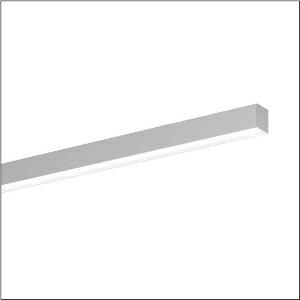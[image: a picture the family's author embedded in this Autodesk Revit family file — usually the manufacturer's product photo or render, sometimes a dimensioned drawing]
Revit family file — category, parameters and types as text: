
# Revit family: silica_r__21_51mx23da44sb_489f
name_source: partatom
category: Lighting Fixtures
units: mm (PartAtom-declared; Revit-internal decimal feet)

## family parameters
Cut with Voids When Loaded = No
Host = Face
Light Source = No
Part Type = Normal
Room Calculation Point = No
Round Connector Dimension = Use Diameter
Shared = No

## types (1)
- --- (1 x LED, 3280 lm, 22.4 W, 4000K)
    Apparent Load = 22 VA
    CIE Flux Codes = 78 96 99 100 100
    Color Rendering = 80
    Color Temperature = 4000K
    Default Elevation = 1800 mm
    Description = Silica® 21, office luminaire, primary optical cover: prismatic diffuser, of PMMA, CAT 2 (L<= 3000cd/m²), light emission: direct distribution, primary light characteristic: symmetric, installation type: surface-mounted, LED, rated luminous flux: 3.280lm, luminous efficacy: 146lm/W, light colour: 840, colour temperature: 4000K, with terminal, 3+2-pole, max. 2.5mm², mains connection: 220..240V, AC, 50/60Hz, rated input power: 22.4W, luminaire housing, of aluminium, metallic grey (RAL 9006), length: 1.204mm, width: 53mm, height: 53mm, protection rating (complete): IP20, insulation class (complete): insulation class I (protective earthing), certification: CE, permissible operating ambient temperature: 0..+35°C, standard: EN 50419, packaging unit: 1 piece
    Height = 0 mm  [stored 0 ft]
    Lamp = 1 x LED
    Lamp Light Flux = 3280 lm
    Lamp Power = 22.4 W
    Lamp count = 1
    Length = 1204 mm
    Luminous efficacy = 146 lm/W
    Manufacturer = Siteco
    ModVariant = No
    Model = 51MX23DA44SB
    Mounting Place = Ceiling
    Mounting Type = Recessed
    Number of Poles = 1
    OnlyDefault = Yes
    Power Factor = 1
    Product Name = Silica® 21
    Product group = office luminaire | ceiling recessed
    ProductGroupID = 401
    Protection Class = Protection class I
    Protection Degree = IP 20
    RLX_Detail_Level = 1
    RLX_Emergency_Light_Flux = 0 lm
    RLX_Emergency_Type = 0
    RLX_Emergency_Type_DB = No
    RlxData = <blob elided: 21213 chars, md5=0b5d6c5e>
    Socket = socket
    Standby Power = 0 W
    System Light Flux = 3280 lm
    System Power = 22 W
    Type Comments = factory setting: luminous flux: 100 % | dim-lin: 254 | 323 mA
    Type Image = l_1297768.jpg
    URL = http://relux.com
    VarID = @adj_049781
    Voltage = 0 V
    Weight = 0.00 kg
    Width = 53 mm

note: [stored X ft] marks values corroborated as IEEE doubles in the binary element streams (Revit-internal decimal feet)

## geometry (parser evidence)
native form markers: Blend x4, Sweep x10
no freeform markers — native parametric forms only
